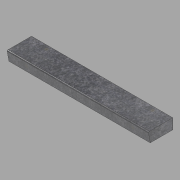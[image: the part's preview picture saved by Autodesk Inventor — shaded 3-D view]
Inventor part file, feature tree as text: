
AUTODESK INVENTOR PART (.ipt)
format: ipt  version: 2022.1 (Build 261234020, 234B)  size: 117,248 bytes
history: native  units: in
note: dims shown in document units (in); Inventor stores cm internally (conversion verified against a paired STEP export)
features: other x3, extrude x1, sketch x1
ambient origin geometry x8: Origin, YZ Plane, XZ Plane, XY Plane, X Axis, Y Axis, Z Axis, Center Point
bodies: Solid1 (feature_tree)
feature tree (5):
  other  "Blocks"
  extrude  "Extrusion1"  Depth=81.375in TaperAngle=0.0deg
  sketch  "Sketch1"  dims[d0=13.0in d1=6.0in d2=13.5in d3=0.5in d4=0.5in d5=81.375in d6=0.0in]
  other  "Profile"
  other  "Profile:1"
